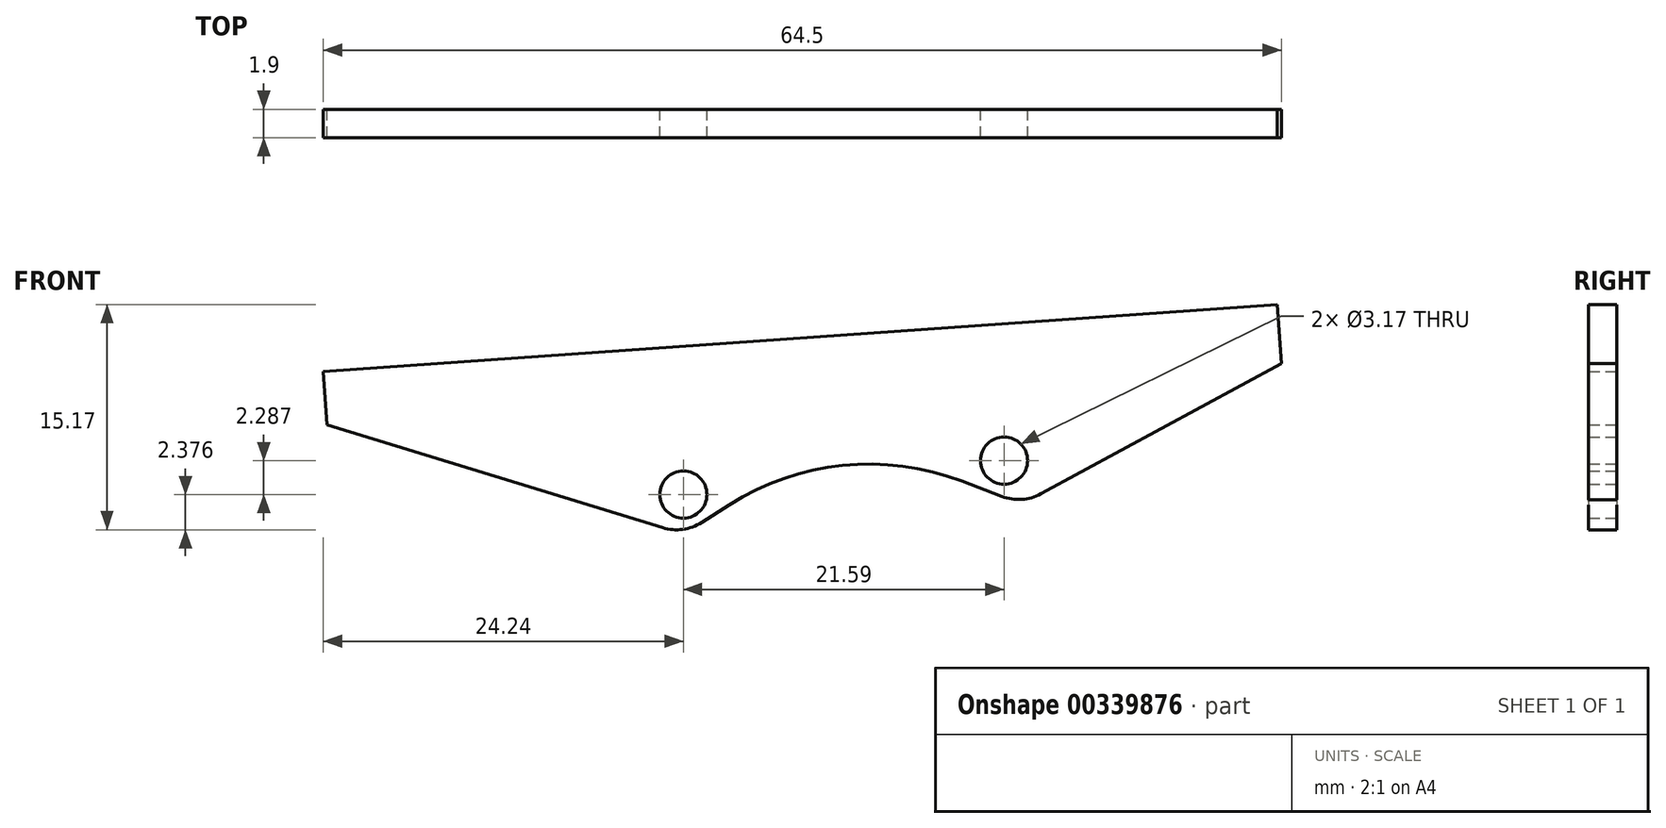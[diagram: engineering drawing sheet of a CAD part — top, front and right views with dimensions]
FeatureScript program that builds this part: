
annotation { "Feature Type Name" : "Feature", "Feature Type Description" : "" }
export const myFeature = defineFeature(function(context is Context, id is Id, definition is map)
    precondition{}
    {
        {
            var Q0;
            Q0=qCreatedBy(makeId("Front.planeOp"),FACE);
            var sketch = newSketch(context, id + "F0", { "sketchPlane" : qUnion([Q0])});
            skCircle(sketch, "E0", {"center": v(-21.59, 9.88) * mm, "radius": 1.59 * mm});
            skCircle(sketch, "E1", {"center": v(0, 12.16) * mm, "radius": 1.59 * mm});
            skArc(sketch, "E2", {"start": v(-18.5, 9.19) * mm, "mid": v(-22.24, 12.98) * mm, "end": v(-24.15, 8) * mm});
            skArc(sketch, "E3", {"start": v(2.33, 10) * mm, "mid": v(0.47, 15.3) * mm, "end": v(-2.86, 10.78) * mm});
            skPoint(sketch, "E4.orphan", {"position": v(18.67, 12.16) * mm});
            skLineSegment(sketch, "E5", {"start": v(-24.15, 8) * mm, "end": v(-45.57, 14.56) * mm});
            skArc(sketch, "E6", {"start": v(-2.86, 10.78) * mm, "mid": v(-10.86, 11.84) * mm, "end": v(-18.5, 9.19) * mm});
            skLineSegment(sketch, "E7", {"start": v(-24.15, 8) * mm, "end": v(-22.99, 7.64) * mm});
            skLineSegment(sketch, "E8", {"start": v(-18.5, 9.19) * mm, "end": v(-20.35, 8) * mm});
            skPoint(sketch, "E9.visualSharp", {"position": v(-21.59, 7.21) * mm});
            skArc(sketch, "E9.filletArc", {"start": v(-22.99, 7.64) * mm, "mid": v(-21.63, 7.53) * mm, "end": v(-20.35, 8) * mm});
            skLineSegment(sketch, "E10", {"start": v(-2.86, 10.78) * mm, "end": v(-0.15, 9.75) * mm});
            skLineSegment(sketch, "E11", {"start": v(18.67, 18.7) * mm, "end": v(2.5, 9.93) * mm});
            skPoint(sketch, "E12.visualSharp", {"position": v(1.21, 9.23) * mm});
            skArc(sketch, "E12.filletArc", {"start": v(-0.15, 9.75) * mm, "mid": v(1.2, 9.55) * mm, "end": v(2.5, 9.93) * mm});
            skLineSegment(sketch, "E13", {"start": v(2.33, 10) * mm, "end": v(2.08, 9.74) * mm});
            skLineSegment(sketch, "E14", {"start": v(18.39, 22.67) * mm, "end": v(-45.83, 18.16) * mm});
            skPoint(sketch, "E15.start.orphan", {"position": v(-46.73, 22.69) * mm});
            skPoint(sketch, "E16.orphan", {"position": v(-46.73, 19.4) * mm});
            skLineSegment(sketch, "E17", {"start": v(-45.83, 18.16) * mm, "end": v(-45.57, 14.56) * mm});
            skPoint(sketch, "E18.orphan", {"position": v(-46.73, 14.92) * mm});
            skPoint(sketch, "E19.orphan", {"position": v(-46.73, 18.1) * mm});
            skLineSegment(sketch, "E20", {"start": v(18.67, 18.7) * mm, "end": v(18.39, 22.69) * mm});
            skSolve(sketch);
        }
        {
            var Q0;
            Q0=makeQuery(id+"F0.imprint","IMPRINT",FACE,{"disambiguationData":[TD([[makeQuery(id+"F0.imprint","IMPRINT",EDGE,{"derivedFrom":sQuery(id+"F0.wireOp",EDGE,"E0")}),-1.0]])]});
            var Q1;
            Q1=makeQuery(id+"F0.imprint","IMPRINT",FACE,{"disambiguationData":[TD([[makeQuery(id+"F0.imprint","IMPRINT",EDGE,{"derivedFrom":sQuery(id+"F0.wireOp",EDGE,"E1")}),-1.0]])]});
            var Q2;
            Q2=makeQuery(id+"F0.imprint","IMPRINT",FACE,{"disambiguationData":[TD([[makeQuery(id+"F0.imprint","IMPRINT",EDGE,{"derivedFrom":sQuery(id+"F0.wireOp",EDGE,"E2")}),-1.0]])]});
            extrude(context, id + "F1", {"entities" : qUnion([Q0, Q1, Q2]), "depth" : 1.9 * mm});
        }
    });
